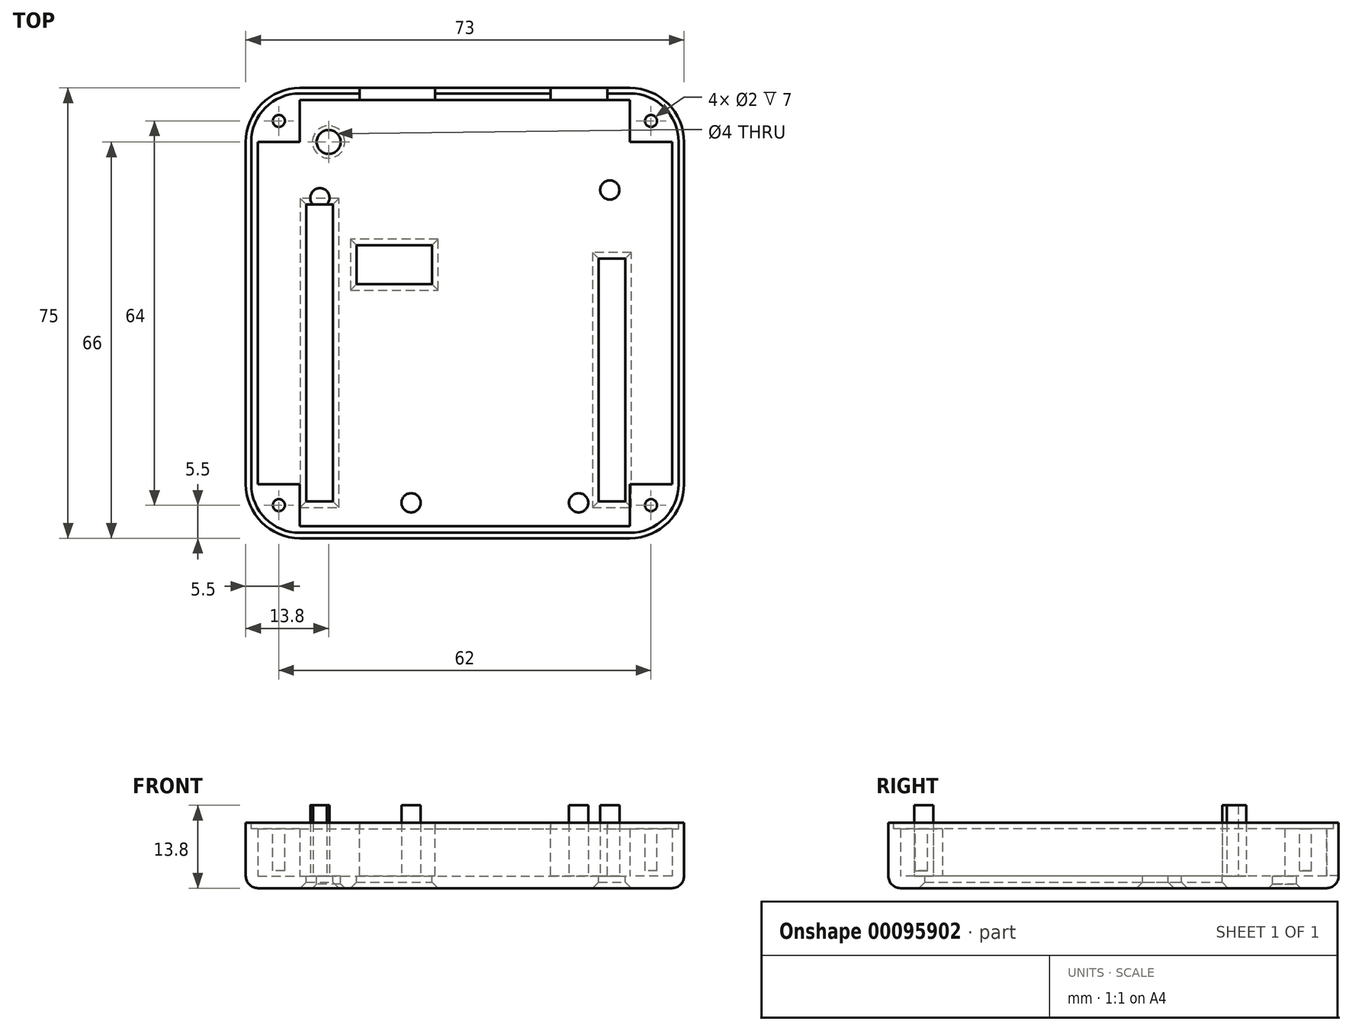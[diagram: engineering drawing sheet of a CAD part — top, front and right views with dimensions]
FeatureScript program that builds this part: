
annotation { "Feature Type Name" : "Feature", "Feature Type Description" : "" }
export const myFeature = defineFeature(function(context is Context, id is Id, definition is map)
    precondition{}
    {
        {
            var Q0;
            Q0=qCreatedBy(makeId("Top.planeOp"),FACE);
            var sketch = newSketch(context, id + "F0", { "sketchPlane" : qUnion([Q0])});
            skLineSegment(sketch, "E0.bottom", {"start": v(-27.5, 38.5) * mm, "end": v(27.5, 38.5) * mm});
            skLineSegment(sketch, "E0.top", {"start": v(-27.5, -36.5) * mm, "end": v(27.5, -36.5) * mm});
            skLineSegment(sketch, "E0.left", {"start": v(-36.5, 29.5) * mm, "end": v(-36.5, -27.5) * mm});
            skLineSegment(sketch, "E0.right", {"start": v(36.5, 29.5) * mm, "end": v(36.5, -27.5) * mm});
            skPoint(sketch, "E1.visualSharp", {"position": v(-36.5, 38.5) * mm});
            skArc(sketch, "E1.filletArc", {"start": v(-27.5, 38.5) * mm, "mid": v(-33.86, 35.86) * mm, "end": v(-36.5, 29.5) * mm});
            skPoint(sketch, "E2.visualSharp", {"position": v(36.5, 38.5) * mm});
            skArc(sketch, "E2.filletArc", {"start": v(36.5, 29.5) * mm, "mid": v(33.86, 35.86) * mm, "end": v(27.5, 38.5) * mm});
            skPoint(sketch, "E3.visualSharp", {"position": v(36.5, -36.5) * mm});
            skArc(sketch, "E3.filletArc", {"start": v(27.5, -36.5) * mm, "mid": v(33.86, -33.86) * mm, "end": v(36.5, -27.5) * mm});
            skPoint(sketch, "E4.visualSharp", {"position": v(-36.5, -36.5) * mm});
            skArc(sketch, "E4.filletArc", {"start": v(-36.5, -27.5) * mm, "mid": v(-33.86, -33.86) * mm, "end": v(-27.5, -36.5) * mm});
            skSolve(sketch);
        }
        {
            var Q0;
            Q0=qSketchRegion(id+"F0",true);
            extrude(context, id + "F1", {"entities" : qUnion([Q0]), "depth" : 2 * mm});
        }
        {
            var Q0;
            Q0=makeQuery(id+"F1.opExtrude","CAP_FACE",FACE,{"disambiguationData":[OSD([sQuery(id+"F0.wireOp",EDGE,"E0.bottom"),sQuery(id+"F0.wireOp",EDGE,"E0.top"),sQuery(id+"F0.wireOp",EDGE,"E0.left"),sQuery(id+"F0.wireOp",EDGE,"E0.right"),sQuery(id+"F0.wireOp",EDGE,"E1.filletArc"),sQuery(id+"F0.wireOp",EDGE,"E2.filletArc"),sQuery(id+"F0.wireOp",EDGE,"E3.filletArc"),sQuery(id+"F0.wireOp",EDGE,"E4.filletArc")])],"isStart":false});
            var sketch = newSketch(context, id + "F2", { "sketchPlane" : qUnion([Q0])});
            skCircle(sketch, "E5.MirrorC", {"center": v(-24.16, 20.2) * mm, "radius": 1.6 * mm});
            skCircle(sketch, "E6.MirrorC", {"center": v(24.14, 21.5) * mm, "radius": 1.6 * mm});
            skCircle(sketch, "E7.MirrorC", {"center": v(18.94, -30.6) * mm, "radius": 1.6 * mm});
            skCircle(sketch, "E8.MirrorC", {"center": v(-8.96, -30.6) * mm, "radius": 1.6 * mm});
            skSolve(sketch);
        }
        {
            var Q0;
            Q0=qSketchRegion(id+"F2",true);
            extrude(context, id + "F3", {"entities" : qUnion([Q0]), "operationType" : NewBodyOperationType.ADD, "depth" : 11.8 * mm});
        }
        {
            var Q0;
            Q0=makeQuery(id+"F1.opExtrude","CAP_FACE",FACE,{"disambiguationData":[OSD([sQuery(id+"F0.wireOp",EDGE,"E0.bottom"),sQuery(id+"F0.wireOp",EDGE,"E0.top"),sQuery(id+"F0.wireOp",EDGE,"E0.left"),sQuery(id+"F0.wireOp",EDGE,"E0.right"),sQuery(id+"F0.wireOp",EDGE,"E1.filletArc"),sQuery(id+"F0.wireOp",EDGE,"E2.filletArc"),sQuery(id+"F0.wireOp",EDGE,"E3.filletArc"),sQuery(id+"F0.wireOp",EDGE,"E4.filletArc")])],"isStart":false});
            var sketch = newSketch(context, id + "F4", { "sketchPlane" : qUnion([Q0])});
            skLineSegment(sketch, "E9", {"start": v(-27.5, 36.5) * mm, "end": v(27.5, 36.5) * mm});
            skLineSegment(sketch, "E10", {"start": v(-34.5, 29.5) * mm, "end": v(-34.5, -27.5) * mm});
            skLineSegment(sketch, "E11", {"start": v(-27.5, -34.5) * mm, "end": v(27.5, -34.5) * mm});
            skLineSegment(sketch, "E12", {"start": v(34.5, -27.5) * mm, "end": v(34.5, 29.5) * mm});
            skArc(sketch, "E13", {"start": v(-27.5, 36.5) * mm, "mid": v(-32.45, 34.45) * mm, "end": v(-34.5, 29.5) * mm});
            skArc(sketch, "E14", {"start": v(27.5, -34.5) * mm, "mid": v(32.45, -32.45) * mm, "end": v(34.5, -27.5) * mm});
            skArc(sketch, "E15", {"start": v(-34.5, -27.5) * mm, "mid": v(-32.45, -32.45) * mm, "end": v(-27.5, -34.5) * mm});
            skArc(sketch, "E16", {"start": v(34.5, 29.5) * mm, "mid": v(32.45, 34.45) * mm, "end": v(27.5, 36.5) * mm});
            skLineSegment(sketch, "E17.0", {"start": v(-27.5, 38.5) * mm, "end": v(27.5, 38.5) * mm});
            skArc(sketch, "E17.1", {"start": v(36.5, 29.5) * mm, "mid": v(33.86, 35.86) * mm, "end": v(27.5, 38.5) * mm});
            skLineSegment(sketch, "E17.2", {"start": v(36.5, 29.5) * mm, "end": v(36.5, -27.5) * mm});
            skArc(sketch, "E17.3", {"start": v(27.5, -36.5) * mm, "mid": v(33.86, -33.86) * mm, "end": v(36.5, -27.5) * mm});
            skLineSegment(sketch, "E17.4", {"start": v(-27.5, -36.5) * mm, "end": v(27.5, -36.5) * mm});
            skArc(sketch, "E17.5", {"start": v(-36.5, -27.5) * mm, "mid": v(-33.86, -33.86) * mm, "end": v(-27.5, -36.5) * mm});
            skLineSegment(sketch, "E17.6", {"start": v(-36.5, 29.5) * mm, "end": v(-36.5, -27.5) * mm});
            skArc(sketch, "E17.7", {"start": v(-27.5, 38.5) * mm, "mid": v(-33.86, 35.86) * mm, "end": v(-36.5, 29.5) * mm});
            skSolve(sketch);
        }
        {
            var Q0;
            Q0=qSketchRegion(id+"F4",true);
            extrude(context, id + "F5", {"entities" : qUnion([Q0]), "operationType" : NewBodyOperationType.ADD, "depth" : 8.9 * mm});
        }
        {
            var Q0;
            Q0=makeQuery(id+"F5.opExtrude","CAP_FACE",FACE,{"disambiguationData":[OSD([sQuery(id+"F4.wireOp",EDGE,"E9"),sQuery(id+"F4.wireOp",EDGE,"E10"),sQuery(id+"F4.wireOp",EDGE,"E11"),sQuery(id+"F4.wireOp",EDGE,"E12"),sQuery(id+"F4.wireOp",EDGE,"E13"),sQuery(id+"F4.wireOp",EDGE,"E14"),sQuery(id+"F4.wireOp",EDGE,"E15"),sQuery(id+"F4.wireOp",EDGE,"E16"),sQuery(id+"F4.wireOp",EDGE,"E17.0"),sQuery(id+"F4.wireOp",EDGE,"E17.1"),sQuery(id+"F4.wireOp",EDGE,"E17.2"),sQuery(id+"F4.wireOp",EDGE,"E17.3"),sQuery(id+"F4.wireOp",EDGE,"E17.4"),sQuery(id+"F4.wireOp",EDGE,"E17.5"),sQuery(id+"F4.wireOp",EDGE,"E17.6"),sQuery(id+"F4.wireOp",EDGE,"E17.7")])],"isStart":false});
            var sketch = newSketch(context, id + "F6", { "sketchPlane" : qUnion([Q0])});
            skLineSegment(sketch, "E18", {"start": v(-27.5, 37.6) * mm, "end": v(27.5, 37.6) * mm});
            skLineSegment(sketch, "E19", {"start": v(-27.5, -35.6) * mm, "end": v(27.5, -35.6) * mm});
            skLineSegment(sketch, "E20", {"start": v(-35.6, 29.5) * mm, "end": v(-35.6, -27.5) * mm});
            skLineSegment(sketch, "E21", {"start": v(35.6, 29.5) * mm, "end": v(35.6, -27.5) * mm});
            skLineSegment(sketch, "E22.0", {"start": v(-27.5, 36.5) * mm, "end": v(27.5, 36.5) * mm});
            skArc(sketch, "E22.1", {"start": v(34.5, 29.5) * mm, "mid": v(32.45, 34.45) * mm, "end": v(27.5, 36.5) * mm});
            skLineSegment(sketch, "E22.2", {"start": v(34.5, -27.5) * mm, "end": v(34.5, 29.5) * mm});
            skArc(sketch, "E22.3", {"start": v(27.5, -34.5) * mm, "mid": v(32.45, -32.45) * mm, "end": v(34.5, -27.5) * mm});
            skLineSegment(sketch, "E22.4", {"start": v(-27.5, -34.5) * mm, "end": v(27.5, -34.5) * mm});
            skArc(sketch, "E22.5", {"start": v(-34.5, -27.5) * mm, "mid": v(-32.45, -32.45) * mm, "end": v(-27.5, -34.5) * mm});
            skLineSegment(sketch, "E22.6", {"start": v(-34.5, 29.5) * mm, "end": v(-34.5, -27.5) * mm});
            skArc(sketch, "E22.7", {"start": v(-27.5, 36.5) * mm, "mid": v(-32.45, 34.45) * mm, "end": v(-34.5, 29.5) * mm});
            skArc(sketch, "E23", {"start": v(-27.5, 37.6) * mm, "mid": v(-33.23, 35.23) * mm, "end": v(-35.6, 29.5) * mm});
            skArc(sketch, "E24", {"start": v(35.6, 29.5) * mm, "mid": v(33.23, 35.23) * mm, "end": v(27.5, 37.6) * mm});
            skArc(sketch, "E25", {"start": v(27.5, -35.6) * mm, "mid": v(33.23, -33.23) * mm, "end": v(35.6, -27.5) * mm});
            skArc(sketch, "E26", {"start": v(-35.6, -27.5) * mm, "mid": v(-33.23, -33.23) * mm, "end": v(-27.5, -35.6) * mm});
            skSolve(sketch);
        }
        {
            var Q0;
            Q0=qSketchRegion(id+"F6",true);
            extrude(context, id + "F7", {"entities" : qUnion([Q0]), "operationType" : NewBodyOperationType.REMOVE, "oppositeDirection" : true, "depth" : 1 * mm});
        }
        {
            var Q0;
            Q0=makeQuery(id+"F5.opExtrude","CAP_FACE",FACE,{"disambiguationData":[OSD([sQuery(id+"F4.wireOp",EDGE,"E9"),sQuery(id+"F4.wireOp",EDGE,"E10"),sQuery(id+"F4.wireOp",EDGE,"E11"),sQuery(id+"F4.wireOp",EDGE,"E12"),sQuery(id+"F4.wireOp",EDGE,"E13"),sQuery(id+"F4.wireOp",EDGE,"E14"),sQuery(id+"F4.wireOp",EDGE,"E15"),sQuery(id+"F4.wireOp",EDGE,"E16"),sQuery(id+"F4.wireOp",EDGE,"E17.0"),sQuery(id+"F4.wireOp",EDGE,"E17.1"),sQuery(id+"F4.wireOp",EDGE,"E17.2"),sQuery(id+"F4.wireOp",EDGE,"E17.3"),sQuery(id+"F4.wireOp",EDGE,"E17.4"),sQuery(id+"F4.wireOp",EDGE,"E17.5"),sQuery(id+"F4.wireOp",EDGE,"E17.6"),sQuery(id+"F4.wireOp",EDGE,"E17.7")])],"isStart":false});
            var sketch = newSketch(context, id + "F8", { "sketchPlane" : qUnion([Q0])});
            skLineSegment(sketch, "E27.bottom", {"start": v(-17.56, 38.5) * mm, "end": v(-4.96, 38.5) * mm});
            skLineSegment(sketch, "E27.top", {"start": v(-17.56, 36.5) * mm, "end": v(-4.96, 36.5) * mm});
            skLineSegment(sketch, "E27.left", {"start": v(-17.56, 38.5) * mm, "end": v(-17.56, 36.5) * mm});
            skLineSegment(sketch, "E27.right", {"start": v(-4.96, 38.5) * mm, "end": v(-4.96, 36.5) * mm});
            skLineSegment(sketch, "E28.bottom", {"start": v(14.24, 38.5) * mm, "end": v(23.74, 38.5) * mm});
            skLineSegment(sketch, "E28.top", {"start": v(14.24, 36.5) * mm, "end": v(23.74, 36.5) * mm});
            skLineSegment(sketch, "E28.left", {"start": v(14.24, 38.5) * mm, "end": v(14.24, 36.5) * mm});
            skLineSegment(sketch, "E28.right", {"start": v(23.74, 38.5) * mm, "end": v(23.74, 36.5) * mm});
            skSolve(sketch);
        }
        {
            var Q0;
            Q0=qSketchRegion(id+"F8",true);
            extrude(context, id + "F9", {"entities" : qUnion([Q0]), "operationType" : NewBodyOperationType.REMOVE, "oppositeDirection" : true, "depth" : 8.8 * mm});
        }
        {
            var Q0;
            Q0=makeQuery(id+"F1.opExtrude","CAP_FACE",FACE,{"disambiguationData":[OSD([sQuery(id+"F0.wireOp",EDGE,"E0.bottom"),sQuery(id+"F0.wireOp",EDGE,"E0.top"),sQuery(id+"F0.wireOp",EDGE,"E0.left"),sQuery(id+"F0.wireOp",EDGE,"E0.right"),sQuery(id+"F0.wireOp",EDGE,"E1.filletArc"),sQuery(id+"F0.wireOp",EDGE,"E2.filletArc"),sQuery(id+"F0.wireOp",EDGE,"E3.filletArc"),sQuery(id+"F0.wireOp",EDGE,"E4.filletArc")])],"isStart":false});
            var sketch = newSketch(context, id + "F10", { "sketchPlane" : qUnion([Q0])});
            skLineSegment(sketch, "E29.bottom", {"start": v(-26.46, 19.1) * mm, "end": v(-21.96, 19.1) * mm});
            skLineSegment(sketch, "E29.top", {"start": v(-26.46, -30.4) * mm, "end": v(-21.96, -30.4) * mm});
            skLineSegment(sketch, "E29.left", {"start": v(-26.46, 19.1) * mm, "end": v(-26.46, -30.4) * mm});
            skLineSegment(sketch, "E29.right", {"start": v(-21.96, 19.1) * mm, "end": v(-21.96, -30.4) * mm});
            skLineSegment(sketch, "E30.bottom", {"start": v(22.24, 10.1) * mm, "end": v(26.74, 10.1) * mm});
            skLineSegment(sketch, "E30.top", {"start": v(22.24, -30.4) * mm, "end": v(26.74, -30.4) * mm});
            skLineSegment(sketch, "E30.left", {"start": v(22.24, 10.1) * mm, "end": v(22.24, -30.4) * mm});
            skLineSegment(sketch, "E30.right", {"start": v(26.74, 10.1) * mm, "end": v(26.74, -30.4) * mm});
            skSolve(sketch);
        }
        {
            var Q0;
            Q0=qSketchRegion(id+"F10",true);
            extrude(context, id + "F11", {"entities" : qUnion([Q0]), "operationType" : NewBodyOperationType.REMOVE, "oppositeDirection" : true, "depth" : 10 * mm});
        }
        {
            var Q0;
            Q0=qSketchRegion(id+"F10",true);
            extrude(context, id + "F12", {"entities" : qUnion([Q0]), "operationType" : NewBodyOperationType.REMOVE, "depth" : 15 * mm});
        }
        {
            var Q0;
            Q0=makeQuery(id+"F1.opExtrude","CAP_FACE",FACE,{"disambiguationData":[OSD([sQuery(id+"F0.wireOp",EDGE,"E0.bottom"),sQuery(id+"F0.wireOp",EDGE,"E0.top"),sQuery(id+"F0.wireOp",EDGE,"E0.left"),sQuery(id+"F0.wireOp",EDGE,"E0.right"),sQuery(id+"F0.wireOp",EDGE,"E1.filletArc"),sQuery(id+"F0.wireOp",EDGE,"E2.filletArc"),sQuery(id+"F0.wireOp",EDGE,"E3.filletArc"),sQuery(id+"F0.wireOp",EDGE,"E4.filletArc")])],"isStart":false});
            var sketch = newSketch(context, id + "F13", { "sketchPlane" : qUnion([Q0])});
            skLineSegment(sketch, "E31", {"start": v(-27.5, 36.5) * mm, "end": v(-27.5, 29.5) * mm});
            skLineSegment(sketch, "E32", {"start": v(-27.5, 29.5) * mm, "end": v(-34.5, 29.5) * mm});
            skArc(sketch, "E33.0", {"start": v(-27.5, 36.5) * mm, "mid": v(-32.45, 34.45) * mm, "end": v(-34.5, 29.5) * mm});
            skArc(sketch, "E33.1", {"start": v(34.5, 29.5) * mm, "mid": v(32.45, 34.45) * mm, "end": v(27.5, 36.5) * mm});
            skArc(sketch, "E33.2", {"start": v(27.5, -34.5) * mm, "mid": v(32.45, -32.45) * mm, "end": v(34.5, -27.5) * mm});
            skArc(sketch, "E33.3", {"start": v(-34.5, -27.5) * mm, "mid": v(-32.45, -32.45) * mm, "end": v(-27.5, -34.5) * mm});
            skLineSegment(sketch, "E34", {"start": v(-34.5, -27.5) * mm, "end": v(-27.5, -27.5) * mm});
            skLineSegment(sketch, "E35", {"start": v(-27.5, -27.5) * mm, "end": v(-27.5, -34.5) * mm});
            skLineSegment(sketch, "E36", {"start": v(34.5, -27.5) * mm, "end": v(27.5, -27.5) * mm});
            skLineSegment(sketch, "E37", {"start": v(27.5, -34.5) * mm, "end": v(27.5, -27.5) * mm});
            skLineSegment(sketch, "E38", {"start": v(27.5, 36.5) * mm, "end": v(27.5, 29.5) * mm});
            skLineSegment(sketch, "E39", {"start": v(34.5, 29.5) * mm, "end": v(27.5, 29.5) * mm});
            skSolve(sketch);
        }
        {
            var Q0;
            Q0=qSketchRegion(id+"F13",true);
            extrude(context, id + "F14", {"entities" : qUnion([Q0]), "operationType" : NewBodyOperationType.ADD, "depth" : 7.9 * mm});
        }
        {
            var Q0;
            {var subQ0=sQuery(id+"F6.wireOp",EDGE,"E18");var subQ1=sQuery(id+"F6.wireOp",EDGE,"E19");var subQ2=sQuery(id+"F6.wireOp",EDGE,"E20");var subQ3=sQuery(id+"F6.wireOp",EDGE,"E21");var subQ4=sQuery(id+"F6.wireOp",EDGE,"E23");var subQ5=sQuery(id+"F6.wireOp",EDGE,"E24");var subQ6=sQuery(id+"F6.wireOp",EDGE,"E25");var subQ7=sQuery(id+"F6.wireOp",EDGE,"E26");Q0=makeQuery(id+"F14.boolean.opBoolean","MERGE",FACE,{"derivedFrom":[makeQuery(id+"F9.boolean.opBoolean","SPLIT",FACE,{"disambiguationData":[TD([makeQuery(id+"F5.opExtrude","SWEPT_FACE",FACE,{"disambiguationData":[OSD([sQuery(id+"F4.wireOp",EDGE,"E10")])]})])],"derivedFrom":makeQuery(id+"F7.boolean.opBoolean","COPY",FACE,{"derivedFrom":makeQuery(id+"F7.opExtrude","CAP_FACE",FACE,{"disambiguationData":[OSD([subQ0,subQ1,subQ2,subQ3,sQuery(id+"F6.wireOp",EDGE,"E22.0"),sQuery(id+"F6.wireOp",EDGE,"E22.1"),sQuery(id+"F6.wireOp",EDGE,"E22.2"),sQuery(id+"F6.wireOp",EDGE,"E22.3"),sQuery(id+"F6.wireOp",EDGE,"E22.4"),sQuery(id+"F6.wireOp",EDGE,"E22.5"),sQuery(id+"F6.wireOp",EDGE,"E22.6"),sQuery(id+"F6.wireOp",EDGE,"E22.7"),subQ4,subQ5,subQ6,subQ7])],"isStart":false})})}),makeQuery(id+"F14.opExtrude","CAP_FACE",FACE,{"disambiguationData":[OSD([sQuery(id+"F13.wireOp",EDGE,"E31"),sQuery(id+"F13.wireOp",EDGE,"E32"),sQuery(id+"F13.wireOp",EDGE,"E33.0")])],"isStart":false}),makeQuery(id+"F14.opExtrude","CAP_FACE",FACE,{"disambiguationData":[OSD([sQuery(id+"F13.wireOp",EDGE,"E33.1"),sQuery(id+"F13.wireOp",EDGE,"E38"),sQuery(id+"F13.wireOp",EDGE,"E39")])],"isStart":false}),makeQuery(id+"F14.opExtrude","CAP_FACE",FACE,{"disambiguationData":[OSD([sQuery(id+"F13.wireOp",EDGE,"E33.2"),sQuery(id+"F13.wireOp",EDGE,"E36"),sQuery(id+"F13.wireOp",EDGE,"E37")])],"isStart":false}),makeQuery(id+"F14.opExtrude","CAP_FACE",FACE,{"disambiguationData":[OSD([sQuery(id+"F13.wireOp",EDGE,"E33.3"),sQuery(id+"F13.wireOp",EDGE,"E34"),sQuery(id+"F13.wireOp",EDGE,"E35")])],"isStart":false})]});}
            var sketch = newSketch(context, id + "F15", { "sketchPlane" : qUnion([Q0])});
            skCircle(sketch, "E40", {"center": v(-31, 33) * mm, "radius": 1 * mm});
            skCircle(sketch, "E41", {"center": v(31, 33) * mm, "radius": 1 * mm});
            skCircle(sketch, "E42", {"center": v(31, -31) * mm, "radius": 1 * mm});
            skCircle(sketch, "E43", {"center": v(-31, -31) * mm, "radius": 1 * mm});
            skSolve(sketch);
        }
        {
            var Q0;
            Q0=qSketchRegion(id+"F15",true);
            extrude(context, id + "F16", {"entities" : qUnion([Q0]), "operationType" : NewBodyOperationType.REMOVE, "oppositeDirection" : true, "depth" : 7 * mm});
        }
        {
            var Q0;
            Q0=makeQuery(id+"F1.opExtrude","CAP_FACE",FACE,{"disambiguationData":[OSD([sQuery(id+"F0.wireOp",EDGE,"E0.bottom"),sQuery(id+"F0.wireOp",EDGE,"E0.top"),sQuery(id+"F0.wireOp",EDGE,"E0.left"),sQuery(id+"F0.wireOp",EDGE,"E0.right"),sQuery(id+"F0.wireOp",EDGE,"E1.filletArc"),sQuery(id+"F0.wireOp",EDGE,"E2.filletArc"),sQuery(id+"F0.wireOp",EDGE,"E3.filletArc"),sQuery(id+"F0.wireOp",EDGE,"E4.filletArc")])],"isStart":false});
            var sketch = newSketch(context, id + "F17", { "sketchPlane" : qUnion([Q0])});
            skLineSegment(sketch, "E44.bottom", {"start": v(-18.06, 12.33) * mm, "end": v(-5.46, 12.33) * mm});
            skLineSegment(sketch, "E44.top", {"start": v(-18.06, 5.83) * mm, "end": v(-5.46, 5.83) * mm});
            skLineSegment(sketch, "E44.left", {"start": v(-18.06, 12.33) * mm, "end": v(-18.06, 5.83) * mm});
            skLineSegment(sketch, "E44.right", {"start": v(-5.46, 12.33) * mm, "end": v(-5.46, 5.83) * mm});
            skSolve(sketch);
        }
        {
            var Q0;
            Q0=qSketchRegion(id+"F17",true);
            extrude(context, id + "F18", {"entities" : qUnion([Q0]), "operationType" : NewBodyOperationType.REMOVE, "oppositeDirection" : true, "depth" : 4 * mm});
        }
        {
            var Q0;
            Q0=makeQuery(id+"F11.boolean.opBoolean","INTERSECT",EDGE,{"derivedFrom":[makeQuery(id+"F1.opExtrude","CAP_FACE",FACE,{"disambiguationData":[OSD([sQuery(id+"F0.wireOp",EDGE,"E0.bottom"),sQuery(id+"F0.wireOp",EDGE,"E0.top"),sQuery(id+"F0.wireOp",EDGE,"E0.left"),sQuery(id+"F0.wireOp",EDGE,"E0.right"),sQuery(id+"F0.wireOp",EDGE,"E1.filletArc"),sQuery(id+"F0.wireOp",EDGE,"E2.filletArc"),sQuery(id+"F0.wireOp",EDGE,"E3.filletArc"),sQuery(id+"F0.wireOp",EDGE,"E4.filletArc")])],"isStart":true}),makeQuery(id+"F11.opExtrude","SWEPT_FACE",FACE,{"disambiguationData":[OSD([sQuery(id+"F10.wireOp",EDGE,"E29.left")])]})]});
            var Q1;
            Q1=makeQuery(id+"F11.boolean.opBoolean","INTERSECT",EDGE,{"derivedFrom":[makeQuery(id+"F1.opExtrude","CAP_FACE",FACE,{"disambiguationData":[OSD([sQuery(id+"F0.wireOp",EDGE,"E0.bottom"),sQuery(id+"F0.wireOp",EDGE,"E0.top"),sQuery(id+"F0.wireOp",EDGE,"E0.left"),sQuery(id+"F0.wireOp",EDGE,"E0.right"),sQuery(id+"F0.wireOp",EDGE,"E1.filletArc"),sQuery(id+"F0.wireOp",EDGE,"E2.filletArc"),sQuery(id+"F0.wireOp",EDGE,"E3.filletArc"),sQuery(id+"F0.wireOp",EDGE,"E4.filletArc")])],"isStart":true}),makeQuery(id+"F11.opExtrude","SWEPT_FACE",FACE,{"disambiguationData":[OSD([sQuery(id+"F10.wireOp",EDGE,"E29.bottom")])]})]});
            var Q2;
            Q2=makeQuery(id+"F11.boolean.opBoolean","INTERSECT",EDGE,{"derivedFrom":[makeQuery(id+"F1.opExtrude","CAP_FACE",FACE,{"disambiguationData":[OSD([sQuery(id+"F0.wireOp",EDGE,"E0.bottom"),sQuery(id+"F0.wireOp",EDGE,"E0.top"),sQuery(id+"F0.wireOp",EDGE,"E0.left"),sQuery(id+"F0.wireOp",EDGE,"E0.right"),sQuery(id+"F0.wireOp",EDGE,"E1.filletArc"),sQuery(id+"F0.wireOp",EDGE,"E2.filletArc"),sQuery(id+"F0.wireOp",EDGE,"E3.filletArc"),sQuery(id+"F0.wireOp",EDGE,"E4.filletArc")])],"isStart":true}),makeQuery(id+"F11.opExtrude","SWEPT_FACE",FACE,{"disambiguationData":[OSD([sQuery(id+"F10.wireOp",EDGE,"E29.right")])]})]});
            var Q3;
            Q3=makeQuery(id+"F11.boolean.opBoolean","INTERSECT",EDGE,{"derivedFrom":[makeQuery(id+"F1.opExtrude","CAP_FACE",FACE,{"disambiguationData":[OSD([sQuery(id+"F0.wireOp",EDGE,"E0.bottom"),sQuery(id+"F0.wireOp",EDGE,"E0.top"),sQuery(id+"F0.wireOp",EDGE,"E0.left"),sQuery(id+"F0.wireOp",EDGE,"E0.right"),sQuery(id+"F0.wireOp",EDGE,"E1.filletArc"),sQuery(id+"F0.wireOp",EDGE,"E2.filletArc"),sQuery(id+"F0.wireOp",EDGE,"E3.filletArc"),sQuery(id+"F0.wireOp",EDGE,"E4.filletArc")])],"isStart":true}),makeQuery(id+"F11.opExtrude","SWEPT_FACE",FACE,{"disambiguationData":[OSD([sQuery(id+"F10.wireOp",EDGE,"E29.top")])]})]});
            var Q4;
            Q4=makeQuery(id+"F18.boolean.opBoolean","INTERSECT",EDGE,{"derivedFrom":[makeQuery(id+"F1.opExtrude","CAP_FACE",FACE,{"disambiguationData":[OSD([sQuery(id+"F0.wireOp",EDGE,"E0.bottom"),sQuery(id+"F0.wireOp",EDGE,"E0.top"),sQuery(id+"F0.wireOp",EDGE,"E0.left"),sQuery(id+"F0.wireOp",EDGE,"E0.right"),sQuery(id+"F0.wireOp",EDGE,"E1.filletArc"),sQuery(id+"F0.wireOp",EDGE,"E2.filletArc"),sQuery(id+"F0.wireOp",EDGE,"E3.filletArc"),sQuery(id+"F0.wireOp",EDGE,"E4.filletArc")])],"isStart":true}),makeQuery(id+"F18.opExtrude","SWEPT_FACE",FACE,{"disambiguationData":[OSD([sQuery(id+"F17.wireOp",EDGE,"E44.top")])]})]});
            var Q5;
            Q5=makeQuery(id+"F18.boolean.opBoolean","INTERSECT",EDGE,{"derivedFrom":[makeQuery(id+"F1.opExtrude","CAP_FACE",FACE,{"disambiguationData":[OSD([sQuery(id+"F0.wireOp",EDGE,"E0.bottom"),sQuery(id+"F0.wireOp",EDGE,"E0.top"),sQuery(id+"F0.wireOp",EDGE,"E0.left"),sQuery(id+"F0.wireOp",EDGE,"E0.right"),sQuery(id+"F0.wireOp",EDGE,"E1.filletArc"),sQuery(id+"F0.wireOp",EDGE,"E2.filletArc"),sQuery(id+"F0.wireOp",EDGE,"E3.filletArc"),sQuery(id+"F0.wireOp",EDGE,"E4.filletArc")])],"isStart":true}),makeQuery(id+"F18.opExtrude","SWEPT_FACE",FACE,{"disambiguationData":[OSD([sQuery(id+"F17.wireOp",EDGE,"E44.left")])]})]});
            var Q6;
            Q6=makeQuery(id+"F18.boolean.opBoolean","INTERSECT",EDGE,{"derivedFrom":[makeQuery(id+"F1.opExtrude","CAP_FACE",FACE,{"disambiguationData":[OSD([sQuery(id+"F0.wireOp",EDGE,"E0.bottom"),sQuery(id+"F0.wireOp",EDGE,"E0.top"),sQuery(id+"F0.wireOp",EDGE,"E0.left"),sQuery(id+"F0.wireOp",EDGE,"E0.right"),sQuery(id+"F0.wireOp",EDGE,"E1.filletArc"),sQuery(id+"F0.wireOp",EDGE,"E2.filletArc"),sQuery(id+"F0.wireOp",EDGE,"E3.filletArc"),sQuery(id+"F0.wireOp",EDGE,"E4.filletArc")])],"isStart":true}),makeQuery(id+"F18.opExtrude","SWEPT_FACE",FACE,{"disambiguationData":[OSD([sQuery(id+"F17.wireOp",EDGE,"E44.bottom")])]})]});
            var Q7;
            Q7=makeQuery(id+"F18.boolean.opBoolean","INTERSECT",EDGE,{"derivedFrom":[makeQuery(id+"F1.opExtrude","CAP_FACE",FACE,{"disambiguationData":[OSD([sQuery(id+"F0.wireOp",EDGE,"E0.bottom"),sQuery(id+"F0.wireOp",EDGE,"E0.top"),sQuery(id+"F0.wireOp",EDGE,"E0.left"),sQuery(id+"F0.wireOp",EDGE,"E0.right"),sQuery(id+"F0.wireOp",EDGE,"E1.filletArc"),sQuery(id+"F0.wireOp",EDGE,"E2.filletArc"),sQuery(id+"F0.wireOp",EDGE,"E3.filletArc"),sQuery(id+"F0.wireOp",EDGE,"E4.filletArc")])],"isStart":true}),makeQuery(id+"F18.opExtrude","SWEPT_FACE",FACE,{"disambiguationData":[OSD([sQuery(id+"F17.wireOp",EDGE,"E44.right")])]})]});
            var Q8;
            Q8=makeQuery(id+"F11.boolean.opBoolean","INTERSECT",EDGE,{"derivedFrom":[makeQuery(id+"F1.opExtrude","CAP_FACE",FACE,{"disambiguationData":[OSD([sQuery(id+"F0.wireOp",EDGE,"E0.bottom"),sQuery(id+"F0.wireOp",EDGE,"E0.top"),sQuery(id+"F0.wireOp",EDGE,"E0.left"),sQuery(id+"F0.wireOp",EDGE,"E0.right"),sQuery(id+"F0.wireOp",EDGE,"E1.filletArc"),sQuery(id+"F0.wireOp",EDGE,"E2.filletArc"),sQuery(id+"F0.wireOp",EDGE,"E3.filletArc"),sQuery(id+"F0.wireOp",EDGE,"E4.filletArc")])],"isStart":true}),makeQuery(id+"F11.opExtrude","SWEPT_FACE",FACE,{"disambiguationData":[OSD([sQuery(id+"F10.wireOp",EDGE,"E30.left")])]})]});
            var Q9;
            Q9=makeQuery(id+"F11.boolean.opBoolean","INTERSECT",EDGE,{"derivedFrom":[makeQuery(id+"F1.opExtrude","CAP_FACE",FACE,{"disambiguationData":[OSD([sQuery(id+"F0.wireOp",EDGE,"E0.bottom"),sQuery(id+"F0.wireOp",EDGE,"E0.top"),sQuery(id+"F0.wireOp",EDGE,"E0.left"),sQuery(id+"F0.wireOp",EDGE,"E0.right"),sQuery(id+"F0.wireOp",EDGE,"E1.filletArc"),sQuery(id+"F0.wireOp",EDGE,"E2.filletArc"),sQuery(id+"F0.wireOp",EDGE,"E3.filletArc"),sQuery(id+"F0.wireOp",EDGE,"E4.filletArc")])],"isStart":true}),makeQuery(id+"F11.opExtrude","SWEPT_FACE",FACE,{"disambiguationData":[OSD([sQuery(id+"F10.wireOp",EDGE,"E30.right")])]})]});
            var Q10;
            Q10=makeQuery(id+"F11.boolean.opBoolean","INTERSECT",EDGE,{"derivedFrom":[makeQuery(id+"F1.opExtrude","CAP_FACE",FACE,{"disambiguationData":[OSD([sQuery(id+"F0.wireOp",EDGE,"E0.bottom"),sQuery(id+"F0.wireOp",EDGE,"E0.top"),sQuery(id+"F0.wireOp",EDGE,"E0.left"),sQuery(id+"F0.wireOp",EDGE,"E0.right"),sQuery(id+"F0.wireOp",EDGE,"E1.filletArc"),sQuery(id+"F0.wireOp",EDGE,"E2.filletArc"),sQuery(id+"F0.wireOp",EDGE,"E3.filletArc"),sQuery(id+"F0.wireOp",EDGE,"E4.filletArc")])],"isStart":true}),makeQuery(id+"F11.opExtrude","SWEPT_FACE",FACE,{"disambiguationData":[OSD([sQuery(id+"F10.wireOp",EDGE,"E30.bottom")])]})]});
            var Q11;
            Q11=makeQuery(id+"F11.boolean.opBoolean","INTERSECT",EDGE,{"derivedFrom":[makeQuery(id+"F1.opExtrude","CAP_FACE",FACE,{"disambiguationData":[OSD([sQuery(id+"F0.wireOp",EDGE,"E0.bottom"),sQuery(id+"F0.wireOp",EDGE,"E0.top"),sQuery(id+"F0.wireOp",EDGE,"E0.left"),sQuery(id+"F0.wireOp",EDGE,"E0.right"),sQuery(id+"F0.wireOp",EDGE,"E1.filletArc"),sQuery(id+"F0.wireOp",EDGE,"E2.filletArc"),sQuery(id+"F0.wireOp",EDGE,"E3.filletArc"),sQuery(id+"F0.wireOp",EDGE,"E4.filletArc")])],"isStart":true}),makeQuery(id+"F11.opExtrude","SWEPT_FACE",FACE,{"disambiguationData":[OSD([sQuery(id+"F10.wireOp",EDGE,"E30.top")])]})]});
            chamfer(context, id + "F19", {"entities" : qUnion([Q0, Q1, Q2, Q3, Q4, Q5, Q6, Q7, Q8, Q9, Q10, Q11]), "width" : 1 * mm, "tangentPropagation" : true});
        }
        {
            var Q0;
            Q0=makeQuery(id+"F1.opExtrude","CAP_FACE",FACE,{"disambiguationData":[OSD([sQuery(id+"F0.wireOp",EDGE,"E0.bottom"),sQuery(id+"F0.wireOp",EDGE,"E0.top"),sQuery(id+"F0.wireOp",EDGE,"E0.left"),sQuery(id+"F0.wireOp",EDGE,"E0.right"),sQuery(id+"F0.wireOp",EDGE,"E1.filletArc"),sQuery(id+"F0.wireOp",EDGE,"E2.filletArc"),sQuery(id+"F0.wireOp",EDGE,"E3.filletArc"),sQuery(id+"F0.wireOp",EDGE,"E4.filletArc")])],"isStart":false});
            var sketch = newSketch(context, id + "F20", { "sketchPlane" : qUnion([Q0])});
            skCircle(sketch, "E45", {"center": v(-22.7, 29.5) * mm, "radius": 2 * mm});
            skSolve(sketch);
        }
        {
            var Q0;
            Q0=qSketchRegion(id+"F20",true);
            extrude(context, id + "F21", {"entities" : qUnion([Q0]), "operationType" : NewBodyOperationType.REMOVE, "oppositeDirection" : true, "depth" : 4 * mm});
        }
        {
            var Q0;
            Q0=makeQuery(id+"F1.opExtrude","CAP_EDGE",EDGE,{"disambiguationData":[OSD([sQuery(id+"F0.wireOp",EDGE,"E0.bottom")])],"isStart":true});
            fillet(context, id + "F22", {"entities" : qUnion([Q0]), "radius" : 2 * mm, "tangentPropagation" : true, "allowEdgeOverflow" : false});
        }
        {
            var Q0;
            Q0=makeQuery(id+"F21.boolean.opBoolean","INTERSECT",EDGE,{"derivedFrom":[makeQuery(id+"F1.opExtrude","CAP_FACE",FACE,{"disambiguationData":[OSD([sQuery(id+"F0.wireOp",EDGE,"E0.bottom"),sQuery(id+"F0.wireOp",EDGE,"E0.top"),sQuery(id+"F0.wireOp",EDGE,"E0.left"),sQuery(id+"F0.wireOp",EDGE,"E0.right"),sQuery(id+"F0.wireOp",EDGE,"E1.filletArc"),sQuery(id+"F0.wireOp",EDGE,"E2.filletArc"),sQuery(id+"F0.wireOp",EDGE,"E3.filletArc"),sQuery(id+"F0.wireOp",EDGE,"E4.filletArc")])],"isStart":true}),makeQuery(id+"F21.opExtrude","SWEPT_FACE",FACE,{"disambiguationData":[OSD([sQuery(id+"F20.wireOp",EDGE,"E45")])]})]});
            chamfer(context, id + "F23", {"entities" : qUnion([Q0]), "width" : .7 * mm, "tangentPropagation" : true});
        }
    });
